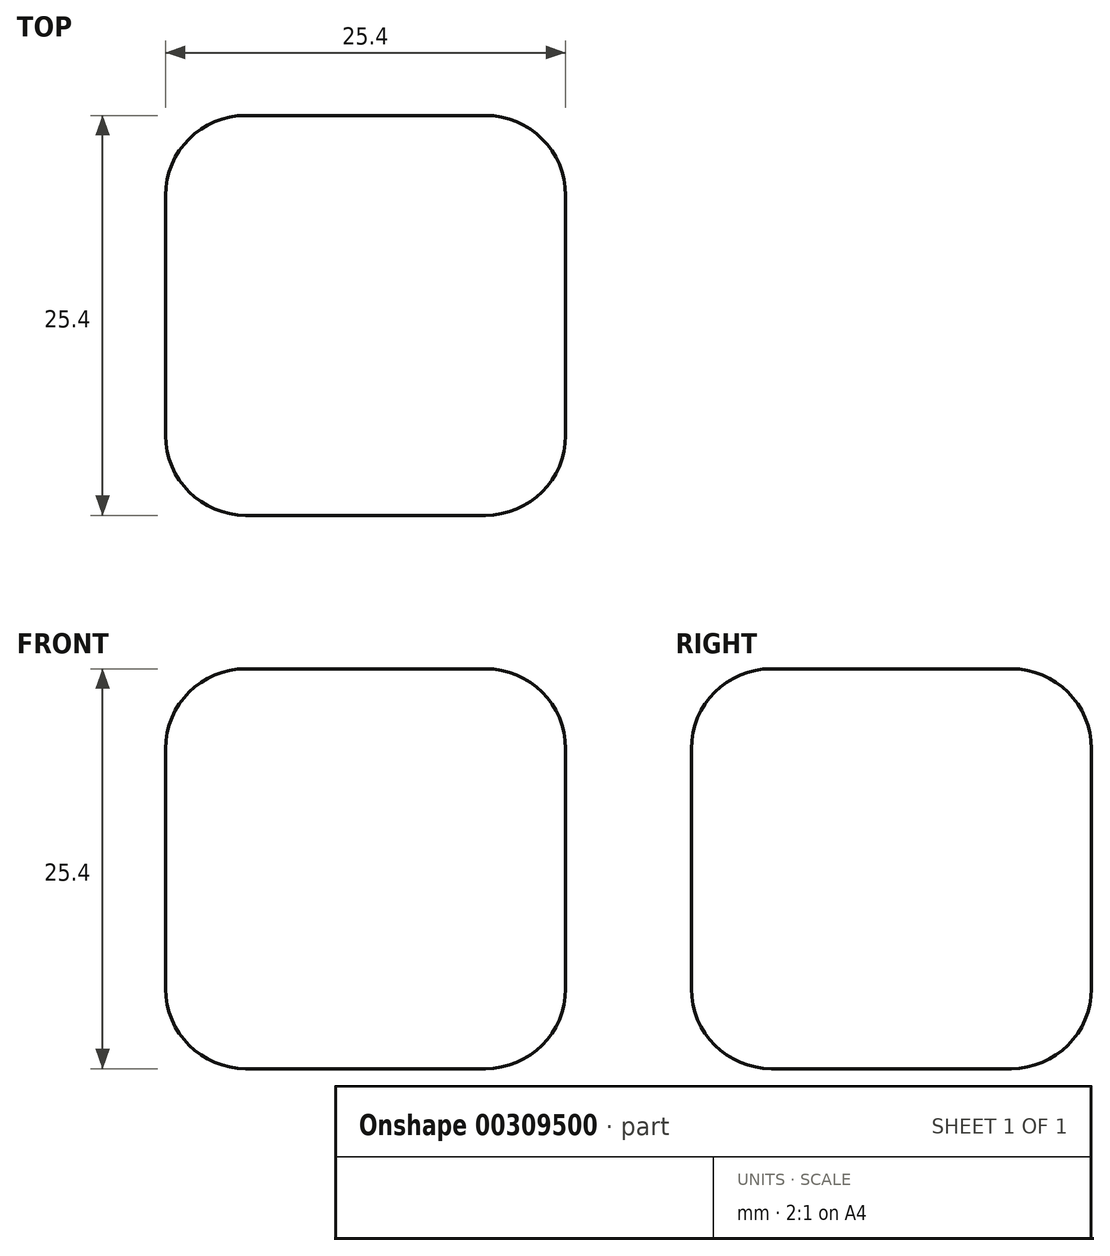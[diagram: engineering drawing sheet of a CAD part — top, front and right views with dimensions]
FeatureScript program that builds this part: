
annotation { "Feature Type Name" : "Feature", "Feature Type Description" : "" }
export const myFeature = defineFeature(function(context is Context, id is Id, definition is map)
    precondition{}
    {
        {
            var Q0;
            Q0=qCreatedBy(makeId("Top.planeOp"),FACE);
            var sketch = newSketch(context, id + "F0", { "sketchPlane" : qUnion([Q0])});
            skLineSegment(sketch, "E0.bottom", {"start": v(-17.32, 18.16) * mm, "end": v(8.08, 18.16) * mm});
            skLineSegment(sketch, "E0.top", {"start": v(-17.32, -7.24) * mm, "end": v(8.08, -7.24) * mm});
            skLineSegment(sketch, "E0.left", {"start": v(-17.32, 18.16) * mm, "end": v(-17.32, -7.24) * mm});
            skLineSegment(sketch, "E0.right", {"start": v(8.08, 18.16) * mm, "end": v(8.08, -7.24) * mm});
            skSolve(sketch);
        }
        {
            var Q0;
            Q0=makeQuery(id+"F0.imprint","IMPRINT",FACE,{"disambiguationData":[TD([[makeQuery(id+"F0.imprint","IMPRINT",EDGE,{"derivedFrom":sQuery(id+"F0.wireOp",EDGE,"E0.bottom")}),-1.0]])]});
            extrude(context, id + "F1", {"entities" : qUnion([Q0]), "depth" : 25.4 * mm});
        }
        {
            var Q0;
            Q0=makeQuery(id+"F1.opExtrude","CAP_EDGE",EDGE,{"disambiguationData":[OSD([sQuery(id+"F0.wireOp",EDGE,"E0.left")])],"isStart":false});
            fillet(context, id + "F2", {"entities" : qUnion([Q0]), "radius" : 5.08 * mm, "tangentPropagation" : true, "allowEdgeOverflow" : false});
        }
        {
            var Q0;
            Q0=makeQuery(id+"F1.opExtrude","CAP_EDGE",EDGE,{"disambiguationData":[OSD([sQuery(id+"F0.wireOp",EDGE,"E0.bottom")])],"isStart":false});
            fillet(context, id + "F3", {"entities" : qUnion([Q0]), "radius" : 5.08 * mm, "tangentPropagation" : true, "allowEdgeOverflow" : false});
        }
        {
            var Q0;
            Q0=makeQuery(id+"F1.opExtrude","CAP_EDGE",EDGE,{"disambiguationData":[OSD([sQuery(id+"F0.wireOp",EDGE,"E0.right")])],"isStart":false});
            fillet(context, id + "F4", {"entities" : qUnion([Q0]), "radius" : 5.08 * mm, "tangentPropagation" : true, "allowEdgeOverflow" : false});
        }
        {
            var Q0;
            Q0=makeQuery(id+"F1.opExtrude","CAP_EDGE",EDGE,{"disambiguationData":[OSD([sQuery(id+"F0.wireOp",EDGE,"E0.top")])],"isStart":false});
            fillet(context, id + "F5", {"entities" : qUnion([Q0]), "radius" : 5.08 * mm, "tangentPropagation" : true, "allowEdgeOverflow" : false});
        }
        {
            var Q0;
            Q0=makeQuery(id+"F1.opExtrude","CAP_EDGE",EDGE,{"disambiguationData":[OSD([sQuery(id+"F0.wireOp",EDGE,"E0.top")])],"isStart":true});
            fillet(context, id + "F6", {"entities" : qUnion([Q0]), "radius" : 5.08 * mm, "tangentPropagation" : true, "allowEdgeOverflow" : false});
        }
    });
